FCSTD DOCUMENT  (FreeCAD 0.18R4 (GitTag))
Label: platform
License: All rights reserved
LicenseURL: http://en.wikipedia.org/wiki/All_rights_reserved
objects: Sketcher::SketchObject×1
note: 1 computed .brp shape members not serialized (recipe doc carries the construction recipe); baked Part::Feature solids carry a one-line shape summary decoded from their .brp

FEATURE [Sketcher::SketchObject] Sketch003  label="Platform"
  sketch-geometry (16):
    g0: LineSegment StartX=-40 StartY=15.5 StartZ=0 EndX=40 EndY=15.5 EndZ=0
    g1: LineSegment StartX=40 StartY=15.5 StartZ=0 EndX=40 EndY=-15.5 EndZ=0
    g2: LineSegment StartX=40 StartY=-15.5 StartZ=0 EndX=-40 EndY=-15.5 EndZ=0
    g3: LineSegment StartX=-40 StartY=-15.5 StartZ=0 EndX=-40 EndY=15.5 EndZ=0
    g4: LineSegment StartX=-36.2042 StartY=6 StartZ=0 EndX=36.2042 EndY=6 EndZ=0
    g5: LineSegment StartX=36.2042 StartY=6 StartZ=0 EndX=36.2042 EndY=-6 EndZ=0
    g6: LineSegment StartX=36.2042 StartY=-6 StartZ=0 EndX=-36.2042 EndY=-6 EndZ=0
    g7: LineSegment StartX=-36.2042 StartY=-6 StartZ=0 EndX=-36.2042 EndY=6 EndZ=0
    g8: ArcOfCircle CenterX=-34.5 CenterY=12.25 CenterZ=0 NormalX=0 NormalY=0 NormalZ=1 AngleXU=0 Radius=1.5 StartAngle=1.5708 EndAngle=4.71239
    g9: ArcOfCircle CenterX=34.5 CenterY=12.25 CenterZ=0 NormalX=0 NormalY=0 NormalZ=1 AngleXU=0 Radius=1.5 StartAngle=4.71239 EndAngle=7.85398
    g10: LineSegment StartX=-34.5 StartY=10.75 StartZ=0 EndX=34.5 EndY=10.75 EndZ=0
    g11: LineSegment StartX=-34.5 StartY=13.75 StartZ=0 EndX=34.5 EndY=13.75 EndZ=0
    g12: ArcOfCircle CenterX=-34.5 CenterY=-12.25 CenterZ=0 NormalX=0 NormalY=0 NormalZ=1 AngleXU=0 Radius=1.5 StartAngle=1.5708 EndAngle=4.71239
    g13: ArcOfCircle CenterX=34.5 CenterY=-12.25 CenterZ=0 NormalX=0 NormalY=0 NormalZ=1 AngleXU=0 Radius=1.5 StartAngle=4.71239 EndAngle=7.85398
    g14: LineSegment StartX=-34.5 StartY=-13.75 StartZ=0 EndX=34.5 EndY=-13.75 EndZ=0
    g15: LineSegment StartX=-34.5 StartY=-10.75 StartZ=0 EndX=34.5 EndY=-10.75 EndZ=0
  constraints (36):
    c: Coincident(g0,g1)
    c: Coincident(g1,g2)
    c: Coincident(g2,g3)
    c: Coincident(g3,g0)
    c: Symmetric(g1,g0,g-1)
    c: Symmetric(g0,g0,g-2)
    c: DistanceX(g0,g0) = 80
    c: DistanceY(g1,g1) = 31
    c: Coincident(g4,g5)
    c: Coincident(g5,g6)
    c: Coincident(g6,g7)
    c: Coincident(g7,g4)
    c: Horizontal(g6)
    c: Vertical(g5)
    c: Symmetric(g2,g0,g-1)
    c: Tangent(g8,g11) = 1.5708
    c: Tangent(g8,g10) = -1.5708
    c: Tangent(g10,g9) = -1.5708
    c: Tangent(g11,g9) = 1.5708
    c: Horizontal(g10)
    c: Tangent(g12,g15) = 1.5708
    c: Tangent(g12,g14) = -1.5708
    c: Tangent(g14,g13) = -1.5708
    c: Tangent(g15,g13) = 1.5708
    c: Horizontal(g14)
    c: DistanceY(g9,g9) = 3
    c: DistanceY(g13,g13) = 3
    c: DistanceY(g13,g9) = 21.5
    c: DistanceY(g7,g7) = 12
    c: Symmetric(g4,g6,g-1)
    c: Symmetric(g4,g4,g-2)
    c: Symmetric(g8,g9,g-2)
    c: Symmetric(g12,g13,g-2)
    c: DistanceX(g11,g11) = 69
    c: DistanceX(g15,g15) = 69
    c: DistanceY(g12,g-1) = 10.75
